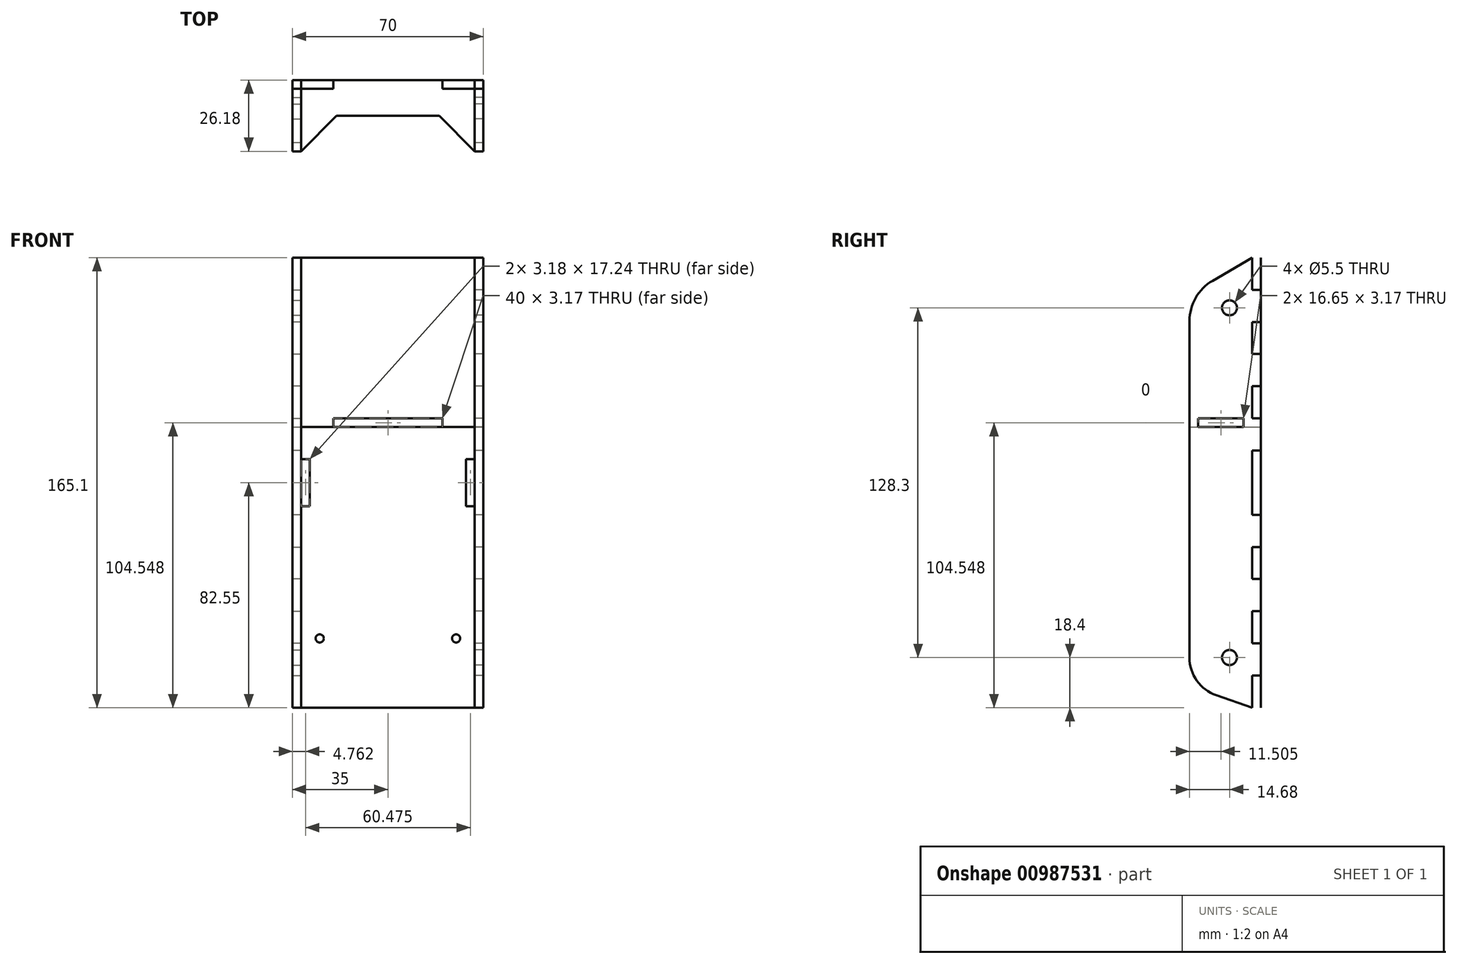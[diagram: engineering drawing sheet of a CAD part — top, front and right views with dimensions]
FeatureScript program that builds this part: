
annotation { "Feature Type Name" : "Feature", "Feature Type Description" : "" }
export const myFeature = defineFeature(function(context is Context, id is Id, definition is map)
    precondition{}
    {
        {
            assignVariable(context, id + "F0", {"name" : "Thickness", "anyValue" : 1 / 203.2 * mm});
        }
        {
            var Q0;
            Q0=qCreatedBy(makeId("Front.planeOp"),FACE);
            var sketch = newSketch(context, id + "F1", { "sketchPlane" : qUnion([Q0])});
            skLineSegment(sketch, "E0", {"start": v(0, 0) * mm, "end": v(-25, 0) * mm, "construction": true});
            skCircle(sketch, "E1", {"center": v(-25, 0) * mm, "radius": 1.5 * mm, "construction": true});
            skLineSegment(sketch, "E2", {"start": v(0, -7) * mm, "end": v(-84.55, -7) * mm, "construction": true});
            skLineSegment(sketch, "E3", {"start": v(0, 139.7) * mm, "end": v(-22.23, 139.7) * mm, "construction": true});
            skLineSegment(sketch, "E4", {"start": v(-22.23, 139.7) * mm, "end": v(-22.22, -25.4) * mm, "construction": true});
            skLineSegment(sketch, "E5", {"start": v(-22.22, -25.4) * mm, "end": v(0, -25.4) * mm, "construction": true});
            skSolve(sketch);
        }
        {
            var Q0;
            Q0=qCreatedBy(makeId("Front.planeOp"),FACE);
            var sketch = newSketch(context, id + "F2", { "sketchPlane" : qUnion([Q0])});
            skCircle(sketch, "E6", {"center": v(-25, 0) * mm, "radius": 1.5 * mm});
            skLineSegment(sketch, "E7", {"start": v(0, -25.4) * mm, "end": v(-35, -25.4) * mm});
            skLineSegment(sketch, "E8", {"start": v(-35, -25.4) * mm, "end": v(-35, -13.6) * mm});
            skLineSegment(sketch, "E9", {"start": v(-35, -13.6) * mm, "end": v(-31.82, -13.6) * mm});
            skLineSegment(sketch, "E10", {"start": v(-31.83, -13.6) * mm, "end": v(-31.83, -1.81) * mm});
            skLineSegment(sketch, "E11", {"start": v(-31.83, -1.81) * mm, "end": v(-35, -1.81) * mm});
            skLineSegment(sketch, "E12.0.1.0", {"start": v(-35, -1.81) * mm, "end": v(-35, 9.98) * mm});
            skLineSegment(sketch, "E12.0.1.1", {"start": v(-31.83, 9.98) * mm, "end": v(-31.83, 21.77) * mm});
            skLineSegment(sketch, "E12.0.1.2", {"start": v(-31.83, 21.77) * mm, "end": v(-35, 21.77) * mm});
            skLineSegment(sketch, "E12.0.1.3", {"start": v(-35, 9.98) * mm, "end": v(-31.83, 9.98) * mm});
            skLineSegment(sketch, "E12.0.2.0", {"start": v(-35, 21.77) * mm, "end": v(-35, 33.56) * mm});
            skLineSegment(sketch, "E12.0.2.1", {"start": v(-31.83, 33.56) * mm, "end": v(-31.83, 45.36) * mm});
            skLineSegment(sketch, "E12.0.2.2", {"start": v(-31.83, 45.36) * mm, "end": v(-35, 45.36) * mm});
            skLineSegment(sketch, "E12.0.2.3", {"start": v(-35, 33.56) * mm, "end": v(-31.83, 33.56) * mm});
            skLineSegment(sketch, "E12.direction1", {"start": v(-35, -25.4) * mm, "end": v(13.37, -25.4) * mm, "construction": true});
            skLineSegment(sketch, "E12.direction2", {"start": v(-35, -25.4) * mm, "end": v(-35, -1.81) * mm, "construction": true});
            skLineSegment(sketch, "E13", {"start": v(-35, 45.36) * mm, "end": v(-35, 57.15) * mm});
            skLineSegment(sketch, "E14", {"start": v(-35, 57.15) * mm, "end": v(-22.23, 57.15) * mm, "construction": true});
            skLineSegment(sketch, "E15.MirrorCS", {"start": v(-35, 80.74) * mm, "end": v(-31.83, 80.74) * mm});
            skLineSegment(sketch, "E16.MirrorCS", {"start": v(-31.83, 116.11) * mm, "end": v(-35, 116.11) * mm});
            skLineSegment(sketch, "E17.MirrorCS", {"start": v(-31.83, 92.53) * mm, "end": v(-35, 92.53) * mm});
            skLineSegment(sketch, "E18.MirrorCS", {"start": v(-35, 127.9) * mm, "end": v(-31.82, 127.9) * mm});
            skLineSegment(sketch, "E19.MirrorCS", {"start": v(-35, 104.32) * mm, "end": v(-31.83, 104.32) * mm});
            skLineSegment(sketch, "E20.MirrorCS", {"start": v(-31.83, 68.94) * mm, "end": v(-35, 68.94) * mm});
            skLineSegment(sketch, "E21.MirrorCS", {"start": v(-31.83, 80.74) * mm, "end": v(-31.83, 68.94) * mm});
            skLineSegment(sketch, "E22.MirrorCS", {"start": v(0, 139.7) * mm, "end": v(-35, 139.7) * mm});
            skLineSegment(sketch, "E23.MirrorCS", {"start": v(-31.83, 104.32) * mm, "end": v(-31.83, 92.53) * mm});
            skLineSegment(sketch, "E24.MirrorCS", {"start": v(-35, 139.7) * mm, "end": v(-35, 127.9) * mm});
            skLineSegment(sketch, "E25.MirrorCS", {"start": v(-35, 92.53) * mm, "end": v(-35, 80.74) * mm});
            skLineSegment(sketch, "E26.MirrorCS", {"start": v(-35, 68.94) * mm, "end": v(-35, 57.15) * mm});
            skLineSegment(sketch, "E27.MirrorCS", {"start": v(-35, 116.11) * mm, "end": v(-35, 104.32) * mm});
            skLineSegment(sketch, "E28.MirrorCS", {"start": v(-31.83, 127.9) * mm, "end": v(-31.83, 116.11) * mm});
            skLineSegment(sketch, "E29", {"start": v(0, 139.7) * mm, "end": v(0, -25.4) * mm, "construction": true});
            skCircle(sketch, "E30.MirrorC", {"center": v(25, 0) * mm, "radius": 1.5 * mm});
            skLineSegment(sketch, "E31.MirrorCS", {"start": v(31.83, -1.81) * mm, "end": v(35, -1.81) * mm});
            skLineSegment(sketch, "E32.MirrorCS", {"start": v(35, -13.6) * mm, "end": v(31.82, -13.6) * mm});
            skLineSegment(sketch, "E33.MirrorCS", {"start": v(35, 80.74) * mm, "end": v(31.83, 80.74) * mm});
            skLineSegment(sketch, "E34.MirrorCS", {"start": v(35, 33.56) * mm, "end": v(31.83, 33.56) * mm});
            skLineSegment(sketch, "E35.MirrorCS", {"start": v(31.83, 21.77) * mm, "end": v(35, 21.77) * mm});
            skLineSegment(sketch, "E36.MirrorCS", {"start": v(35, 127.9) * mm, "end": v(31.82, 127.9) * mm});
            skLineSegment(sketch, "E37.MirrorCS", {"start": v(31.83, 116.11) * mm, "end": v(35, 116.11) * mm});
            skLineSegment(sketch, "E38.MirrorCS", {"start": v(35, 9.98) * mm, "end": v(31.83, 9.98) * mm});
            skLineSegment(sketch, "E39.MirrorCS", {"start": v(31.83, 92.53) * mm, "end": v(35, 92.53) * mm});
            skLineSegment(sketch, "E40.MirrorCS", {"start": v(31.83, 45.36) * mm, "end": v(35, 45.36) * mm});
            skLineSegment(sketch, "E41.MirrorCS", {"start": v(31.83, 68.94) * mm, "end": v(35, 68.94) * mm});
            skLineSegment(sketch, "E42.MirrorCS", {"start": v(35, 104.32) * mm, "end": v(31.83, 104.32) * mm});
            skLineSegment(sketch, "E43.MirrorCS", {"start": v(35, 57.15) * mm, "end": v(22.23, 57.15) * mm, "construction": true});
            skLineSegment(sketch, "E44.MirrorCS", {"start": v(35, 116.11) * mm, "end": v(35, 104.32) * mm});
            skLineSegment(sketch, "E45.MirrorCS", {"start": v(31.83, 9.98) * mm, "end": v(31.83, 21.77) * mm});
            skLineSegment(sketch, "E46.MirrorCS", {"start": v(35, -25.4) * mm, "end": v(35, -13.6) * mm});
            skLineSegment(sketch, "E47.MirrorCS", {"start": v(31.83, -13.6) * mm, "end": v(31.83, -1.81) * mm});
            skLineSegment(sketch, "E48.MirrorCS", {"start": v(35, 68.94) * mm, "end": v(35, 57.15) * mm});
            skLineSegment(sketch, "E49.MirrorCS", {"start": v(35, 92.53) * mm, "end": v(35, 80.74) * mm});
            skLineSegment(sketch, "E50.MirrorCS", {"start": v(35, 21.77) * mm, "end": v(35, 33.56) * mm});
            skLineSegment(sketch, "E51.MirrorCS", {"start": v(31.83, 104.32) * mm, "end": v(31.83, 92.53) * mm});
            skLineSegment(sketch, "E52.MirrorCS", {"start": v(31.83, 127.9) * mm, "end": v(31.83, 116.11) * mm});
            skLineSegment(sketch, "E53.MirrorCS", {"start": v(31.83, 80.74) * mm, "end": v(31.83, 68.94) * mm});
            skLineSegment(sketch, "E54.MirrorCS", {"start": v(0, -25.4) * mm, "end": v(35, -25.4) * mm});
            skLineSegment(sketch, "E55.MirrorCS", {"start": v(31.83, 33.56) * mm, "end": v(31.83, 45.36) * mm});
            skLineSegment(sketch, "E56.MirrorCS", {"start": v(0, 139.7) * mm, "end": v(35, 139.7) * mm});
            skLineSegment(sketch, "E57.MirrorCS", {"start": v(35, 139.7) * mm, "end": v(35, 127.9) * mm});
            skLineSegment(sketch, "E58.MirrorCS", {"start": v(35, -1.81) * mm, "end": v(35, 9.98) * mm});
            skLineSegment(sketch, "E59.MirrorCS", {"start": v(35, 45.36) * mm, "end": v(35, 57.15) * mm});
            skLineSegment(sketch, "E60.bottom", {"start": v(31.83, 65.77) * mm, "end": v(28.65, 65.77) * mm});
            skLineSegment(sketch, "E60.top", {"start": v(31.83, 48.53) * mm, "end": v(28.65, 48.53) * mm});
            skLineSegment(sketch, "E60.left", {"start": v(31.83, 65.77) * mm, "end": v(31.83, 48.53) * mm});
            skLineSegment(sketch, "E60.right", {"start": v(28.65, 65.77) * mm, "end": v(28.65, 48.53) * mm});
            skPoint(sketch, "E61", {"position": v(31.83, 57.15) * mm});
            skLineSegment(sketch, "E62.MirrorCS", {"start": v(-28.65, 65.77) * mm, "end": v(-28.65, 48.53) * mm});
            skLineSegment(sketch, "E63.MirrorCS", {"start": v(-31.83, 65.77) * mm, "end": v(-31.83, 48.53) * mm});
            skLineSegment(sketch, "E64.MirrorCS", {"start": v(-31.83, 48.53) * mm, "end": v(-28.65, 48.53) * mm});
            skLineSegment(sketch, "E65.MirrorCS", {"start": v(-31.83, 65.77) * mm, "end": v(-28.65, 65.77) * mm});
            skPoint(sketch, "E66.MirrorP", {"position": v(-31.83, 57.15) * mm});
            skLineSegment(sketch, "E67.bottom", {"start": v(20, 80.74) * mm, "end": v(-20, 80.74) * mm});
            skLineSegment(sketch, "E67.top", {"start": v(20, 77.56) * mm, "end": v(-20, 77.56) * mm});
            skLineSegment(sketch, "E67.left", {"start": v(20, 80.74) * mm, "end": v(20, 77.56) * mm});
            skLineSegment(sketch, "E67.right", {"start": v(-20, 80.74) * mm, "end": v(-20, 77.56) * mm});
            skPoint(sketch, "E68", {"position": v(0, 80.74) * mm});
            skSolve(sketch);
        }
        {
            var Q0;
            Q0 = qSketchRegion(id + "F2", true);
            extrude(context, id + "F3", {"entities" : qUnion([Q0]), "depth" : getVariable(context, 'Thickness'), "offsetDistance" : 25 * mm});
        }
        {
            var Q0;
            Q0=qCreatedBy(makeId("Right.planeOp"),FACE);
            var sketch = newSketch(context, id + "F4", { "sketchPlane" : qUnion([Q0])});
            skLineSegment(sketch, "E69", {"start": v(-3.18, 57.15) * mm, "end": v(0, 57.15) * mm, "construction": true});
            skLineSegment(sketch, "E70", {"start": v(-3.18, -25.4) * mm, "end": v(-3.18, -13.6) * mm});
            skLineSegment(sketch, "E71", {"start": v(-3.17, -13.6) * mm, "end": v(0, -13.6) * mm});
            skLineSegment(sketch, "E72", {"start": v(0, -13.6) * mm, "end": v(0, -1.81) * mm});
            skLineSegment(sketch, "E73", {"start": v(0, -1.81) * mm, "end": v(-3.18, -1.81) * mm});
            skLineSegment(sketch, "E74.0.1.0", {"start": v(-3.18, -1.81) * mm, "end": v(-3.18, 9.98) * mm});
            skLineSegment(sketch, "E74.0.1.1", {"start": v(0, 9.98) * mm, "end": v(0, 21.77) * mm});
            skLineSegment(sketch, "E74.0.1.2", {"start": v(0, 21.77) * mm, "end": v(-3.18, 21.77) * mm});
            skLineSegment(sketch, "E74.0.1.3", {"start": v(-3.18, 9.98) * mm, "end": v(0, 9.98) * mm});
            skLineSegment(sketch, "E74.0.2.0", {"start": v(-3.18, 21.77) * mm, "end": v(-3.18, 33.56) * mm});
            skLineSegment(sketch, "E74.0.2.1", {"start": v(0, 33.56) * mm, "end": v(0, 45.36) * mm});
            skLineSegment(sketch, "E74.0.2.2", {"start": v(0, 45.36) * mm, "end": v(-3.18, 45.36) * mm});
            skLineSegment(sketch, "E74.0.2.3", {"start": v(-3.18, 33.56) * mm, "end": v(0, 33.56) * mm});
            skLineSegment(sketch, "E74.direction1", {"start": v(-3.18, -25.4) * mm, "end": v(21.82, -25.4) * mm, "construction": true});
            skLineSegment(sketch, "E74.direction2", {"start": v(-3.18, -25.4) * mm, "end": v(-3.18, -1.81) * mm, "construction": true});
            skLineSegment(sketch, "E75", {"start": v(-3.18, 45.36) * mm, "end": v(-3.18, 57.15) * mm});
            skLineSegment(sketch, "E76.MirrorCS", {"start": v(-3.18, 104.32) * mm, "end": v(0, 104.32) * mm});
            skLineSegment(sketch, "E77.MirrorCS", {"start": v(0, 68.94) * mm, "end": v(-3.18, 68.94) * mm});
            skLineSegment(sketch, "E78.MirrorCS", {"start": v(0, 116.11) * mm, "end": v(-3.18, 116.11) * mm});
            skLineSegment(sketch, "E79.MirrorCS", {"start": v(-3.17, 127.9) * mm, "end": v(0, 127.9) * mm});
            skLineSegment(sketch, "E80.MirrorCS", {"start": v(0, 92.53) * mm, "end": v(-3.18, 92.53) * mm});
            skLineSegment(sketch, "E81.MirrorCS", {"start": v(-3.18, 80.74) * mm, "end": v(0, 80.74) * mm});
            skLineSegment(sketch, "E82.MirrorCS", {"start": v(0, 104.32) * mm, "end": v(0, 92.53) * mm});
            skLineSegment(sketch, "E83.MirrorCS", {"start": v(-3.18, 116.11) * mm, "end": v(-3.18, 104.32) * mm});
            skLineSegment(sketch, "E84.MirrorCS", {"start": v(-3.18, 92.53) * mm, "end": v(-3.18, 80.74) * mm});
            skLineSegment(sketch, "E85.MirrorCS", {"start": v(0, 80.74) * mm, "end": v(0, 68.94) * mm});
            skLineSegment(sketch, "E86.MirrorCS", {"start": v(0, 127.9) * mm, "end": v(0, 116.11) * mm});
            skLineSegment(sketch, "E87.MirrorCS", {"start": v(-3.18, 68.94) * mm, "end": v(-3.18, 57.15) * mm});
            skLineSegment(sketch, "E88.MirrorCS", {"start": v(-3.18, 139.7) * mm, "end": v(-3.18, 127.9) * mm});
            skLineSegment(sketch, "E89", {"start": v(-3.18, 139.7) * mm, "end": v(-17.67, 131.24) * mm});
            skLineSegment(sketch, "E90", {"start": v(-3.17, -25.4) * mm, "end": v(-16.29, -20.87) * mm});
            skArc(sketch, "E91", {"start": v(-17.67, 131.24) * mm, "mid": v(-23.9, 124.97) * mm, "end": v(-26.18, 116.42) * mm});
            skArc(sketch, "E92", {"start": v(-16.29, -20.87) * mm, "mid": v(-23.45, -15.52) * mm, "end": v(-26.17, -7) * mm});
            skLineSegment(sketch, "E93", {"start": v(-26.18, 116.42) * mm, "end": v(-26.17, -7) * mm});
            skLineSegment(sketch, "E94", {"start": v(0, -7) * mm, "end": v(-11.5, -7) * mm, "construction": true});
            skCircle(sketch, "E95", {"center": v(-11.5, -7) * mm, "radius": 2.75 * mm});
            skCircle(sketch, "E96.MirrorC", {"center": v(-11.5, 121.3) * mm, "radius": 2.75 * mm});
            skLineSegment(sketch, "E97.bottom", {"start": v(-23, 80.74) * mm, "end": v(-6.35, 80.74) * mm});
            skLineSegment(sketch, "E97.top", {"start": v(-23, 77.56) * mm, "end": v(-6.35, 77.56) * mm});
            skLineSegment(sketch, "E97.left", {"start": v(-23, 80.74) * mm, "end": v(-23, 77.56) * mm});
            skLineSegment(sketch, "E97.right", {"start": v(-6.35, 80.74) * mm, "end": v(-6.35, 77.56) * mm});
            skSolve(sketch);
        }
        {
            var Q0;
            Q0=makeQuery(id+"F4.imprint","IMPRINT",FACE,{"disambiguationData":[TD([[makeQuery(id+"F4.imprint","IMPRINT",EDGE,{"derivedFrom":sQuery(id+"F4.wireOp",EDGE,"E70")}),1.0]])]});
            var Q1;
            Q1 = qConstructionFilter(qBodyType(qCreatedBy(id + "F4" ,EDGE), BodyType.WIRE), ConstructionObject.NO);
            var Q2;
            Q2=makeQuery(id+"F3.opExtrude","CAP_VERTEX",VERTEX,{"disambiguationData":[OSD([sQuery(id+"F2.wireOp",EDGE,"E46.MirrorCS"),sQuery(id+"F2.wireOp",EDGE,"E54.MirrorCS")])],"isStart":false});
            var Q3;
            Q3=makeQuery(id+"F3.opExtrude","CAP_VERTEX",VERTEX,{"disambiguationData":[OSD([sQuery(id+"F2.wireOp",EDGE,"E32.MirrorCS"),sQuery(id+"F2.wireOp",EDGE,"E47.MirrorCS")])],"isStart":false});
            extrude(context, id + "F5", {"entities" : qUnion([Q0]), "surfaceEntities" : qUnion([Q1]), "endBound" : BoundingType.UP_TO_VERTEX, "depth" : 25 * mm, "endBoundEntityVertex" : qUnion([Q2]), "offsetDistance" : 25 * mm, "hasSecondDirection" : true, "secondDirectionBound" : SecondDirectionBoundingType.UP_TO_VERTEX, "secondDirectionOppositeDirection" : false, "secondDirectionDepth" : 25 * mm, "secondDirectionBoundEntityVertex" : qUnion([Q3])});
        }
        {
            var Q0;
            Q0=makeQuery(id+"F5.opExtrude","SWEPT_BODY",BODY,{"disambiguationData":[OSD([sQuery(id+"F4.wireOp",EDGE,"E70"),sQuery(id+"F4.wireOp",EDGE,"E71"),sQuery(id+"F4.wireOp",EDGE,"E72"),sQuery(id+"F4.wireOp",EDGE,"E73"),sQuery(id+"F4.wireOp",EDGE,"E74.0.1.0"),sQuery(id+"F4.wireOp",EDGE,"E74.0.1.1"),sQuery(id+"F4.wireOp",EDGE,"E74.0.1.2"),sQuery(id+"F4.wireOp",EDGE,"E74.0.1.3"),sQuery(id+"F4.wireOp",EDGE,"E74.0.2.0"),sQuery(id+"F4.wireOp",EDGE,"E74.0.2.1"),sQuery(id+"F4.wireOp",EDGE,"E74.0.2.2"),sQuery(id+"F4.wireOp",EDGE,"E74.0.2.3"),sQuery(id+"F4.wireOp",EDGE,"E75"),sQuery(id+"F4.wireOp",EDGE,"E76.MirrorCS"),sQuery(id+"F4.wireOp",EDGE,"E77.MirrorCS"),sQuery(id+"F4.wireOp",EDGE,"E78.MirrorCS"),sQuery(id+"F4.wireOp",EDGE,"E79.MirrorCS"),sQuery(id+"F4.wireOp",EDGE,"E80.MirrorCS"),sQuery(id+"F4.wireOp",EDGE,"E81.MirrorCS"),sQuery(id+"F4.wireOp",EDGE,"E82.MirrorCS"),sQuery(id+"F4.wireOp",EDGE,"E83.MirrorCS"),sQuery(id+"F4.wireOp",EDGE,"E84.MirrorCS"),sQuery(id+"F4.wireOp",EDGE,"E85.MirrorCS"),sQuery(id+"F4.wireOp",EDGE,"E86.MirrorCS"),sQuery(id+"F4.wireOp",EDGE,"E87.MirrorCS"),sQuery(id+"F4.wireOp",EDGE,"E88.MirrorCS"),sQuery(id+"F4.wireOp",EDGE,"E89"),sQuery(id+"F4.wireOp",EDGE,"E90"),sQuery(id+"F4.wireOp",EDGE,"E91"),sQuery(id+"F4.wireOp",EDGE,"E92"),sQuery(id+"F4.wireOp",EDGE,"E93"),sQuery(id+"F4.wireOp",EDGE,"E95"),sQuery(id+"F4.wireOp",EDGE,"E96.MirrorC")])]});
            var Q1;
            Q1=qCreatedBy(makeId("Right.planeOp"),FACE);
            mirror(context, id + "F6", {"entities" : qUnion([Q0]), "mirrorPlane" : qUnion([Q1])});
        }
        {
            var Q0;
            Q0=makeQuery(id+"F3.opExtrude","SWEPT_FACE",FACE,{"disambiguationData":[OSD([sQuery(id+"F2.wireOp",EDGE,"E67.top")])]});
            var sketch = newSketch(context, id + "F7", { "sketchPlane" : qUnion([Q0])});
            skLineSegment(sketch, "E98", {"start": v(0, -3.18) * mm, "end": v(0, -40.2) * mm, "construction": true});
            skLineSegment(sketch, "E99", {"start": v(0, -13.17) * mm, "end": v(-18.82, -13.18) * mm});
            skLineSegment(sketch, "E100", {"start": v(-18.82, -13.18) * mm, "end": v(-31.82, -26.18) * mm});
            skLineSegment(sketch, "E101", {"start": v(-31.82, -26.18) * mm, "end": v(-31.82, -23) * mm});
            skLineSegment(sketch, "E102", {"start": v(-31.82, -23) * mm, "end": v(-35, -23) * mm});
            skLineSegment(sketch, "E103", {"start": v(-35, -23) * mm, "end": v(-35, -6.35) * mm});
            skLineSegment(sketch, "E104", {"start": v(-35, -6.35) * mm, "end": v(-31.82, -6.35) * mm});
            skLineSegment(sketch, "E105", {"start": v(-31.82, -6.35) * mm, "end": v(-31.82, -3.18) * mm});
            skLineSegment(sketch, "E106", {"start": v(-31.82, -3.18) * mm, "end": v(-20, -3.18) * mm});
            skLineSegment(sketch, "E107", {"start": v(-20, -3.18) * mm, "end": v(-20, 0) * mm});
            skLineSegment(sketch, "E108", {"start": v(-20, 0) * mm, "end": v(0, 0) * mm});
            skLineSegment(sketch, "E109.MirrorCS", {"start": v(20, -3.18) * mm, "end": v(20, 0) * mm});
            skLineSegment(sketch, "E110.MirrorCS", {"start": v(31.82, -23) * mm, "end": v(35, -23) * mm});
            skLineSegment(sketch, "E111.MirrorCS", {"start": v(35, -6.35) * mm, "end": v(31.82, -6.35) * mm});
            skLineSegment(sketch, "E112.MirrorCS", {"start": v(31.82, -26.18) * mm, "end": v(31.82, -23) * mm});
            skLineSegment(sketch, "E113.MirrorCS", {"start": v(31.82, -6.35) * mm, "end": v(31.82, -3.18) * mm});
            skLineSegment(sketch, "E114.MirrorCS", {"start": v(31.82, -3.18) * mm, "end": v(20, -3.18) * mm});
            skLineSegment(sketch, "E115.MirrorCS", {"start": v(20, 0) * mm, "end": v(0, 0) * mm});
            skLineSegment(sketch, "E116.MirrorCS", {"start": v(35, -23) * mm, "end": v(35, -6.35) * mm});
            skLineSegment(sketch, "E117.MirrorCS", {"start": v(18.82, -13.18) * mm, "end": v(31.82, -26.18) * mm});
            skLineSegment(sketch, "E118.MirrorCS", {"start": v(0, -13.17) * mm, "end": v(18.82, -13.18) * mm});
            skSolve(sketch);
        }
        {
            var Q0;
            Q0 = qSketchRegion(id + "F7", true);
            extrude(context, id + "F8", {"entities" : qUnion([Q0]), "depth" : getVariable(context, 'Thickness'), "offsetDistance" : 25 * mm});
        }
    });
